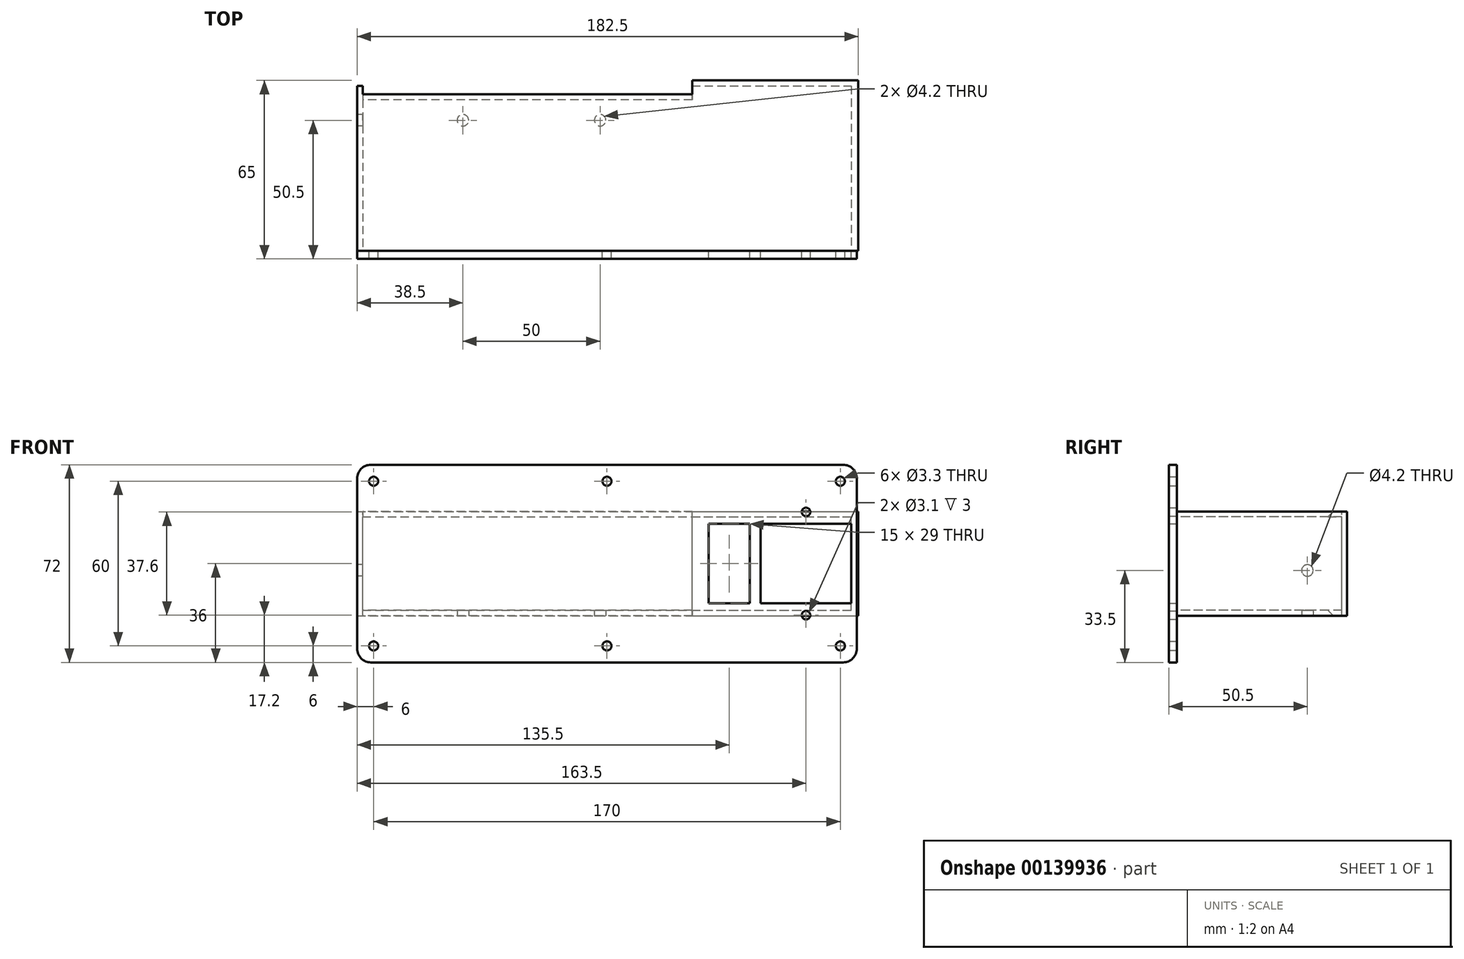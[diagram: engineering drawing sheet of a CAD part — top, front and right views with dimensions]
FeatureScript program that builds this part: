
annotation { "Feature Type Name" : "Feature", "Feature Type Description" : "" }
export const myFeature = defineFeature(function(context is Context, id is Id, definition is map)
    precondition{}
    {
        {
            var Q0;
            Q0=qCreatedBy(makeId("Front.planeOp"),FACE);
            var sketch = newSketch(context, id + "F0", { "sketchPlane" : qUnion([Q0])});
            skLineSegment(sketch, "E0.bottom", {"start": v(-86, 72) * mm, "end": v(86, 72) * mm});
            skLineSegment(sketch, "E0.top", {"start": v(-86, 0) * mm, "end": v(86, 0) * mm});
            skLineSegment(sketch, "E0.left", {"start": v(-91, 67) * mm, "end": v(-91, 5) * mm});
            skLineSegment(sketch, "E0.right", {"start": v(91, 67) * mm, "end": v(91, 5) * mm});
            skPoint(sketch, "E1", {"position": v(0, 0) * mm});
            skPoint(sketch, "E2.visualSharp", {"position": v(-91, 72) * mm});
            skArc(sketch, "E2.filletArc", {"start": v(-86, 72) * mm, "mid": v(-89.54, 70.54) * mm, "end": v(-91, 67) * mm});
            skPoint(sketch, "E3.visualSharp", {"position": v(91, 72) * mm});
            skArc(sketch, "E3.filletArc", {"start": v(91, 67) * mm, "mid": v(89.54, 70.54) * mm, "end": v(86, 72) * mm});
            skPoint(sketch, "E4.visualSharp", {"position": v(-91, 0) * mm});
            skArc(sketch, "E4.filletArc", {"start": v(-91, 5) * mm, "mid": v(-89.54, 1.46) * mm, "end": v(-86, 0) * mm});
            skPoint(sketch, "E5.visualSharp", {"position": v(91, 0) * mm});
            skArc(sketch, "E5.filletArc", {"start": v(86, 0) * mm, "mid": v(89.54, 1.46) * mm, "end": v(91, 5) * mm});
            skCircle(sketch, "E6", {"center": v(-85, 66) * mm, "radius": 1.65 * mm});
            skCircle(sketch, "E7", {"center": v(85, 66) * mm, "radius": 1.65 * mm});
            skCircle(sketch, "E8", {"center": v(-85, 6) * mm, "radius": 1.65 * mm});
            skCircle(sketch, "E9", {"center": v(85, 6) * mm, "radius": 1.65 * mm});
            skLineSegment(sketch, "E10.bottom", {"start": v(89, 50.5) * mm, "end": v(56, 50.5) * mm});
            skLineSegment(sketch, "E10.top", {"start": v(89, 21.5) * mm, "end": v(56, 21.5) * mm});
            skLineSegment(sketch, "E10.left", {"start": v(89, 50.5) * mm, "end": v(89, 21.5) * mm});
            skLineSegment(sketch, "E10.right", {"start": v(56, 50.5) * mm, "end": v(56, 21.5) * mm});
            skLineSegment(sketch, "E11.bottom", {"start": v(37, 50.5) * mm, "end": v(52, 50.5) * mm});
            skLineSegment(sketch, "E11.top", {"start": v(37, 21.5) * mm, "end": v(52, 21.5) * mm});
            skLineSegment(sketch, "E11.left", {"start": v(37, 50.5) * mm, "end": v(37, 21.5) * mm});
            skLineSegment(sketch, "E11.right", {"start": v(52, 50.5) * mm, "end": v(52, 21.5) * mm});
            skLineSegment(sketch, "E12.bottom", {"start": v(-85, 51) * mm, "end": v(30, 51) * mm, "construction": true});
            skLineSegment(sketch, "E12.top", {"start": v(-85, 21) * mm, "end": v(30, 21) * mm, "construction": true});
            skLineSegment(sketch, "E12.left", {"start": v(-85, 51) * mm, "end": v(-85, 21) * mm, "construction": true});
            skLineSegment(sketch, "E12.right", {"start": v(30, 51) * mm, "end": v(30, 21) * mm, "construction": true});
            skLineSegment(sketch, "E13", {"start": v(-91, 17) * mm, "end": v(91, 17) * mm, "construction": true});
            skLineSegment(sketch, "E14", {"start": v(91, 55) * mm, "end": v(-91, 55) * mm, "construction": true});
            skCircle(sketch, "E15", {"center": v(72.5, 17.2) * mm, "radius": 1.55 * mm});
            skCircle(sketch, "E16", {"center": v(72.5, 54.8) * mm, "radius": 1.55 * mm});
            skCircle(sketch, "E17", {"center": v(0, 66) * mm, "radius": 1.65 * mm});
            skCircle(sketch, "E18", {"center": v(0, 6) * mm, "radius": 1.65 * mm});
            skPoint(sketch, "E19", {"position": v(-91, 36) * mm});
            skPoint(sketch, "E20", {"position": v(-85, 36) * mm});
            skPoint(sketch, "E21", {"position": v(37, 36) * mm});
            skPoint(sketch, "E22", {"position": v(72.5, 50.5) * mm});
            skLineSegment(sketch, "E23", {"start": v(72.5, 50.5) * mm, "end": v(72.5, 55) * mm, "construction": true});
            skLineSegment(sketch, "E24", {"start": v(72.5, 21.5) * mm, "end": v(72.5, 17) * mm, "construction": true});
            skSolve(sketch);
        }
        {
            var Q0;
            Q0=makeQuery(id+"F0.imprint","IMPRINT",FACE,{"disambiguationData":[TD([[makeQuery(id+"F0.imprint","IMPRINT",EDGE,{"derivedFrom":sQuery(id+"F0.wireOp",EDGE,"E0.bottom")}),-1.0]])]});
            extrude(context, id + "F1", {"entities" : qUnion([Q0]), "depth" : 3 * mm});
        }
        {
            var Q0;
            Q0=makeQuery(id+"F0.imprint","IMPRINT",FACE,{"disambiguationData":[TD([[makeQuery(id+"F0.imprint","IMPRINT",EDGE,{"derivedFrom":sQuery(id+"F0.wireOp",EDGE,"E0.bottom")}),-1.0]])]});
            var sketch = newSketch(context, id + "F2", { "sketchPlane" : qUnion([Q0])});
            skLineSegment(sketch, "E25.bottom", {"start": v(-91, 17) * mm, "end": v(91.5, 17) * mm});
            skLineSegment(sketch, "E25.top", {"start": v(-91, 55) * mm, "end": v(91.5, 55) * mm});
            skLineSegment(sketch, "E25.left", {"start": v(-91, 17) * mm, "end": v(-91, 55) * mm});
            skLineSegment(sketch, "E25.right", {"start": v(91.5, 17) * mm, "end": v(91.5, 55) * mm});
            skLineSegment(sketch, "E26.bottom", {"start": v(-89, 19) * mm, "end": v(89, 19) * mm});
            skLineSegment(sketch, "E26.top", {"start": v(-89, 53) * mm, "end": v(89, 53) * mm});
            skLineSegment(sketch, "E26.left", {"start": v(-89, 19) * mm, "end": v(-89, 53) * mm});
            skLineSegment(sketch, "E26.right", {"start": v(89, 19) * mm, "end": v(89, 53) * mm});
            skSolve(sketch);
        }
        {
            var Q0;
            Q0 = qSketchRegion(id + "F2", true);
            extrude(context, id + "F3", {"entities" : qUnion([Q0]), "operationType" : NewBodyOperationType.ADD, "oppositeDirection" : true, "depth" : 60 * mm});
        }
        {
            var Q0;
            Q0=makeQuery(id+"F3.opExtrude","SWEPT_FACE",FACE,{"disambiguationData":[OSD([sQuery(id+"F2.wireOp",EDGE,"E25.bottom")])]});
            var sketch = newSketch(context, id + "F4", { "sketchPlane" : qUnion([Q0])});
            skCircle(sketch, "E27", {"center": v(-52.5, -47.5) * mm, "radius": 2.1 * mm});
            skCircle(sketch, "E28", {"center": v(-2.5, -47.5) * mm, "radius": 2.1 * mm});
            skLineSegment(sketch, "E29", {"start": v(30, 0) * mm, "end": v(-2.5, 0) * mm, "construction": true});
            skLineSegment(sketch, "E30", {"start": v(-2.5, 0) * mm, "end": v(-52.5, 0) * mm, "construction": true});
            skLineSegment(sketch, "E31", {"start": v(-52.5, 0) * mm, "end": v(-85, 0) * mm, "construction": true});
            skSolve(sketch);
        }
        {
            var Q0;
            Q0 = qSketchRegion(id + "F4", true);
            extrude(context, id + "F5", {"entities" : qUnion([Q0]), "operationType" : NewBodyOperationType.REMOVE, "oppositeDirection" : true, "depth" : 25 * mm});
        }
        {
            var Q0;
            Q0=makeQuery(id+"F3.boolean.opBoolean","MERGE",FACE,{"derivedFrom":[makeQuery(id+"F1.opExtrude","SWEPT_FACE",FACE,{"disambiguationData":[OSD([sQuery(id+"F0.wireOp",EDGE,"E0.left")])]}),makeQuery(id+"F3.opExtrude","SWEPT_FACE",FACE,{"disambiguationData":[OSD([sQuery(id+"F2.wireOp",EDGE,"E25.left")])]})]});
            var sketch = newSketch(context, id + "F6", { "sketchPlane" : qUnion([Q0])});
            skCircle(sketch, "E32", {"center": v(-47.5, 33.5) * mm, "radius": 2.1 * mm});
            skSolve(sketch);
        }
        {
            var Q0;
            Q0 = qSketchRegion(id + "F6", true);
            extrude(context, id + "F7", {"entities" : qUnion([Q0]), "operationType" : NewBodyOperationType.REMOVE, "oppositeDirection" : true, "depth" : 25 * mm});
        }
        {
            var Q0;
            Q0=makeQuery(id+"F3.opExtrude","CAP_FACE",FACE,{"disambiguationData":[OSD([sQuery(id+"F2.wireOp",EDGE,"E25.bottom"),sQuery(id+"F2.wireOp",EDGE,"E25.top"),sQuery(id+"F2.wireOp",EDGE,"E25.left"),sQuery(id+"F2.wireOp",EDGE,"E25.right"),sQuery(id+"F2.wireOp",EDGE,"E26.bottom"),sQuery(id+"F2.wireOp",EDGE,"E26.top"),sQuery(id+"F2.wireOp",EDGE,"E26.left"),sQuery(id+"F2.wireOp",EDGE,"E26.right")])],"isStart":false});
            var sketch = newSketch(context, id + "F8", { "sketchPlane" : qUnion([Q0])});
            skLineSegment(sketch, "E33.bottom", {"start": v(-91.5, 17) * mm, "end": v(-31, 17) * mm});
            skLineSegment(sketch, "E33.top", {"start": v(-91.5, 55) * mm, "end": v(-31, 55) * mm});
            skLineSegment(sketch, "E33.left", {"start": v(-91.5, 17) * mm, "end": v(-91.5, 55) * mm});
            skLineSegment(sketch, "E33.right", {"start": v(-31, 17) * mm, "end": v(-31, 55) * mm});
            skSolve(sketch);
        }
        {
            var Q0;
            Q0 = qSketchRegion(id + "F8", true);
            extrude(context, id + "F9", {"entities" : qUnion([Q0]), "operationType" : NewBodyOperationType.ADD, "depth" : 2 * mm});
        }
        {
            var Q0;
            Q0=makeQuery(id+"F3.opExtrude","CAP_EDGE",EDGE,{"disambiguationData":[OSD([sQuery(id+"F2.wireOp",EDGE,"E26.right")])],"isStart":false});
            var Q1;
            {var subQ0=sQuery(id+"F2.wireOp",EDGE,"E26.top");Q1=makeQuery(id+"F9.boolean.opBoolean","SPLIT",EDGE,{"disambiguationData":[TD([makeQuery(id+"F1.opExtrude","SWEPT_FACE",FACE,{"disambiguationData":[OSD([sQuery(id+"F0.wireOp",EDGE,"E10.left")])]})])],"derivedFrom":makeQuery(id+"F3.opExtrude","CAP_EDGE",EDGE,{"disambiguationData":[OSD([subQ0])],"isStart":false})});}
            var Q2;
            {var subQ0=sQuery(id+"F2.wireOp",EDGE,"E26.bottom");Q2=makeQuery(id+"F9.boolean.opBoolean","SPLIT",EDGE,{"disambiguationData":[TD([makeQuery(id+"F1.opExtrude","SWEPT_FACE",FACE,{"disambiguationData":[OSD([sQuery(id+"F0.wireOp",EDGE,"E10.left")])]})])],"derivedFrom":makeQuery(id+"F3.opExtrude","CAP_EDGE",EDGE,{"disambiguationData":[OSD([subQ0])],"isStart":false})});}
            chamfer(context, id + "F10", {"entities" : qUnion([Q0, Q1, Q2]), "width" : 5 * mm, "tangentPropagation" : true});
        }
    });
